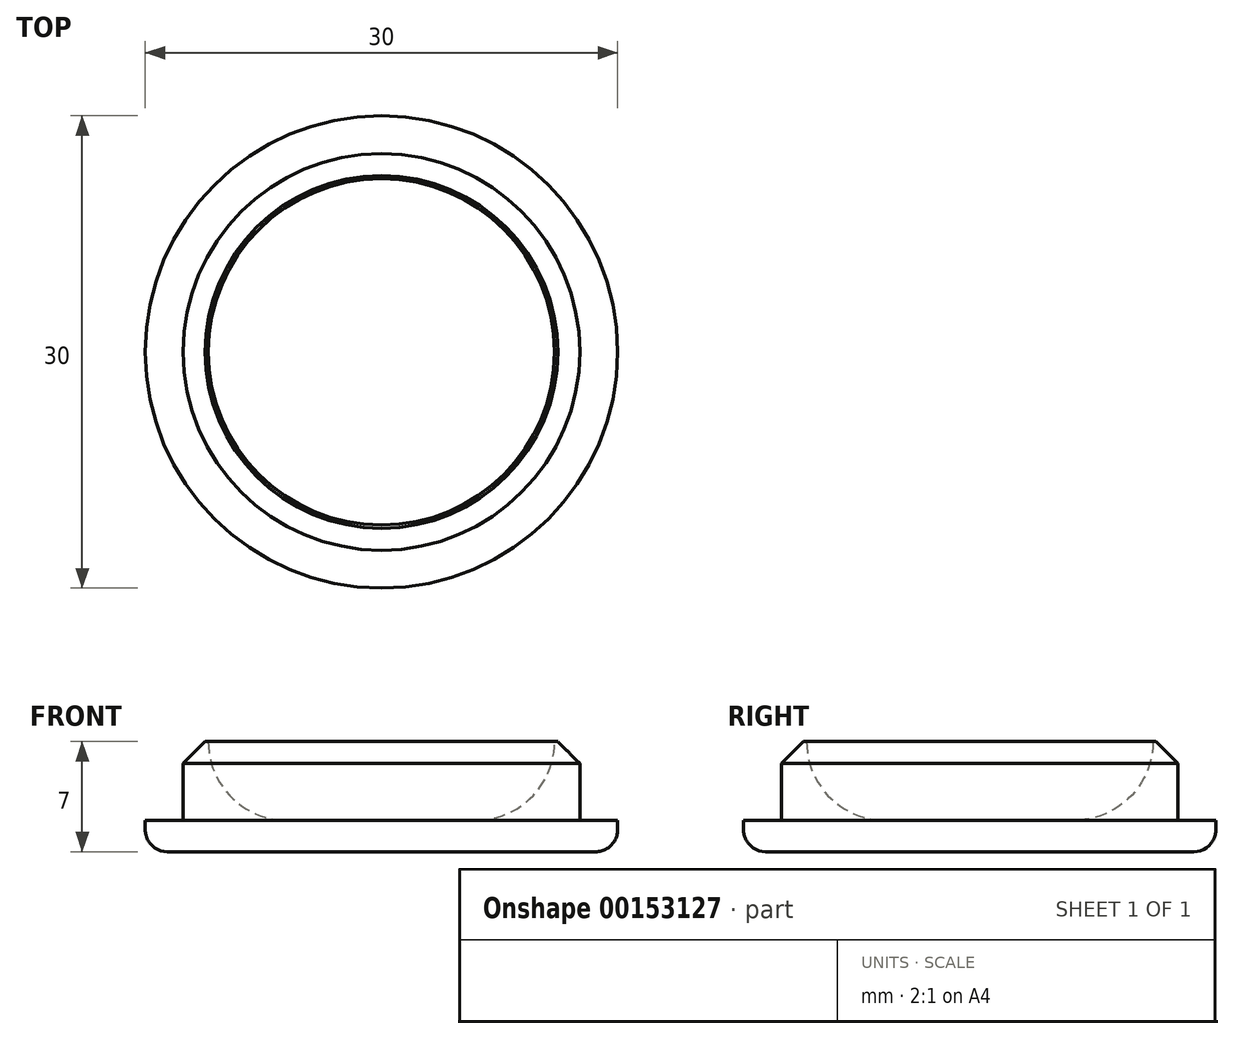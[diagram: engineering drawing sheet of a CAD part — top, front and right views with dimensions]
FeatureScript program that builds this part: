
annotation { "Feature Type Name" : "Feature", "Feature Type Description" : "" }
export const myFeature = defineFeature(function(context is Context, id is Id, definition is map)
    precondition{}
    {
        {
            var Q0;
            Q0=qCreatedBy(makeId("Top.planeOp"),FACE);
            var sketch = newSketch(context, id + "F0", { "sketchPlane" : qUnion([Q0])});
            skCircle(sketch, "E0", {"center": v(0, 0) * mm, "radius": 15 * mm});
            skCircle(sketch, "E1", {"center": v(0, 0) * mm, "radius": 13 * mm});
            skCircle(sketch, "E2", {"center": v(0, 0) * mm, "radius": 11 * mm});
            skCircle(sketch, "E3.0", {"center": v(0, 0) * mm, "radius": 12.6 * mm});
            skSolve(sketch);
        }
        {
            var Q0;
            Q0=makeQuery(id+"F0.imprint","IMPRINT",FACE,{"disambiguationData":[TD([[makeQuery(id+"F0.imprint","IMPRINT",EDGE,{"derivedFrom":sQuery(id+"F0.wireOp",EDGE,"E2")}),1.0]])]});
            var Q1;
            Q1=makeQuery(id+"F0.imprint","IMPRINT",FACE,{"disambiguationData":[TD([[makeQuery(id+"F0.imprint","IMPRINT",EDGE,{"derivedFrom":sQuery(id+"F0.wireOp",EDGE,"E2")}),-1.0]])]});
            var Q2;
            Q2=makeQuery(id+"F0.imprint","IMPRINT",FACE,{"disambiguationData":[TD([[makeQuery(id+"F0.imprint","IMPRINT",EDGE,{"derivedFrom":sQuery(id+"F0.wireOp",EDGE,"E1")}),1.0]])]});
            var Q3;
            Q3=makeQuery(id+"F0.imprint","IMPRINT",FACE,{"disambiguationData":[TD([[makeQuery(id+"F0.imprint","IMPRINT",EDGE,{"derivedFrom":sQuery(id+"F0.wireOp",EDGE,"E0")}),1.0]])]});
            extrude(context, id + "F1", {"entities" : qUnion([Q0, Q1, Q2, Q3]), "depth" : 2 * mm});
        }
        {
            var Q0;
            Q0=makeQuery(id+"F0.imprint","IMPRINT",FACE,{"disambiguationData":[TD([[makeQuery(id+"F0.imprint","IMPRINT",EDGE,{"derivedFrom":sQuery(id+"F0.wireOp",EDGE,"E2")}),-1.0]])]});
            extrude(context, id + "F2", {"entities" : qUnion([Q0]), "operationType" : NewBodyOperationType.ADD, "depth" : 7 * mm});
        }
        {
            var Q0;
            Q0=makeQuery(id+"F2.boolean.opBoolean","INTERSECT",EDGE,{"derivedFrom":[makeQuery(id+"F1.opExtrude","CAP_FACE",FACE,{"disambiguationData":[OSD([sQuery(id+"F0.wireOp",EDGE,"E0")])],"isStart":false}),makeQuery(id+"F2.opExtrude","SWEPT_FACE",FACE,{"disambiguationData":[OSD([sQuery(id+"F0.wireOp",EDGE,"E2")])]})]});
            fillet(context, id + "F3", {"entities" : qUnion([Q0]), "radius" : 5 * mm, "tangentPropagation" : true, "allowEdgeOverflow" : false});
        }
        {
            var Q0;
            Q0=makeQuery(id+"F2.opExtrude","CAP_EDGE",EDGE,{"disambiguationData":[OSD([sQuery(id+"F0.wireOp",EDGE,"E3.0")])],"isStart":false});
            chamfer(context, id + "F4", {"entities" : qUnion([Q0]), "width" : 1.4 * mm, "tangentPropagation" : true});
        }
        {
            var Q0;
            Q0=makeQuery(id+"F1.opExtrude","CAP_EDGE",EDGE,{"disambiguationData":[OSD([sQuery(id+"F0.wireOp",EDGE,"E0")])],"isStart":true});
            fillet(context, id + "F5", {"entities" : qUnion([Q0]), "radius" : 1.4 * mm, "tangentPropagation" : true, "allowEdgeOverflow" : false});
        }
    });
